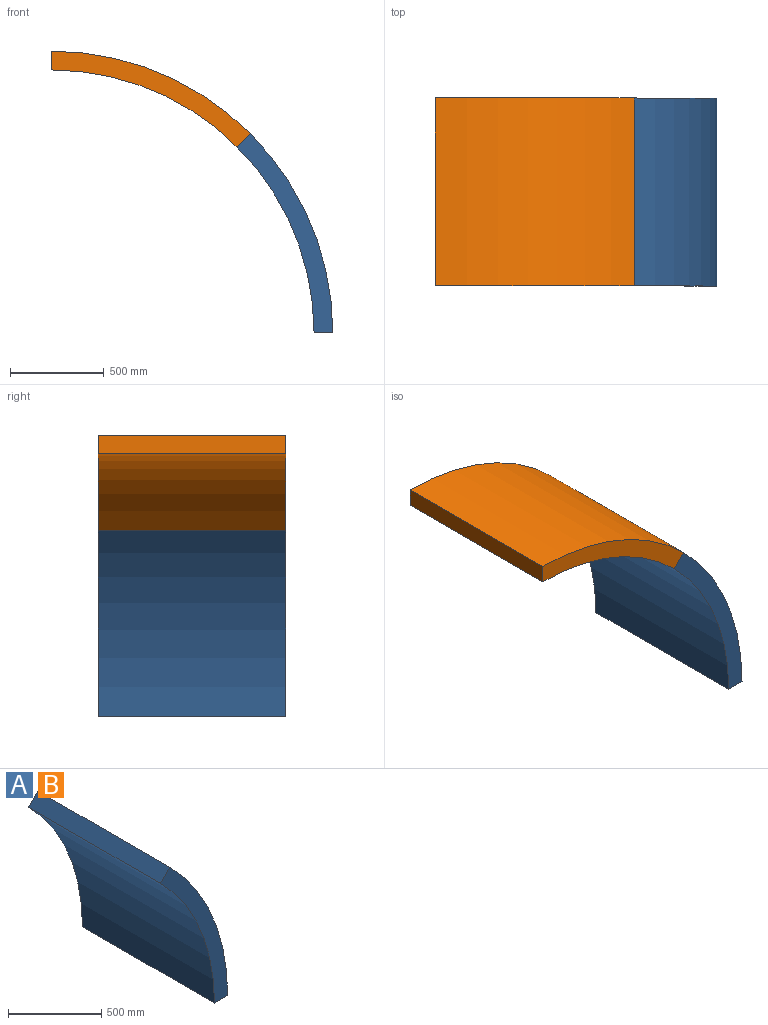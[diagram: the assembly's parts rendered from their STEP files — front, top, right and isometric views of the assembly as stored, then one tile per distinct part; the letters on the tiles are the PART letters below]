
ASSEMBLY  parts=2 mates=1
PART A: 6 faces, bbox 510.1x1000x1060.7 mm
  f0: cylinder r=1400mm len=1000mm, axis (0,1,0), area 1099557.4mm2, adj f1,f3,f4,f5
  f1: plane 1000x100mm, normal (0,0,-1), area 100000mm2, adj f0,f2,f4,f5
  f2: cylinder r=1500mm len=1060.66mm, axis (0,1,0), area 1178097.2mm2, adj f1,f3,f4,f5
  f3: plane 1000x70.71mm, normal (-0.71,0,0.71), area 100000mm2, adj f0,f2,f4,f5
  f4: plane 1060.66x510.05mm, normal (0,-1,0), area 113882.7mm2, adj f0,f1,f2,f3
  f5: plane 1060.66x510.05mm, normal (0,1,0), area 113882.7mm2, adj f0,f1,f2,f3
PART B: same geometry as A
PLACE A t=(-1174.13,367.5,-790.43)mm
PLACE B rot(axis=(0,-1,0),45deg) t=(-1174.13,367.5,-790.43)mm
MATE fastened B.f1 <-> A.f3  axis (0.71,0,-0.71) through (-148.83,-132.5,234.88)mm
